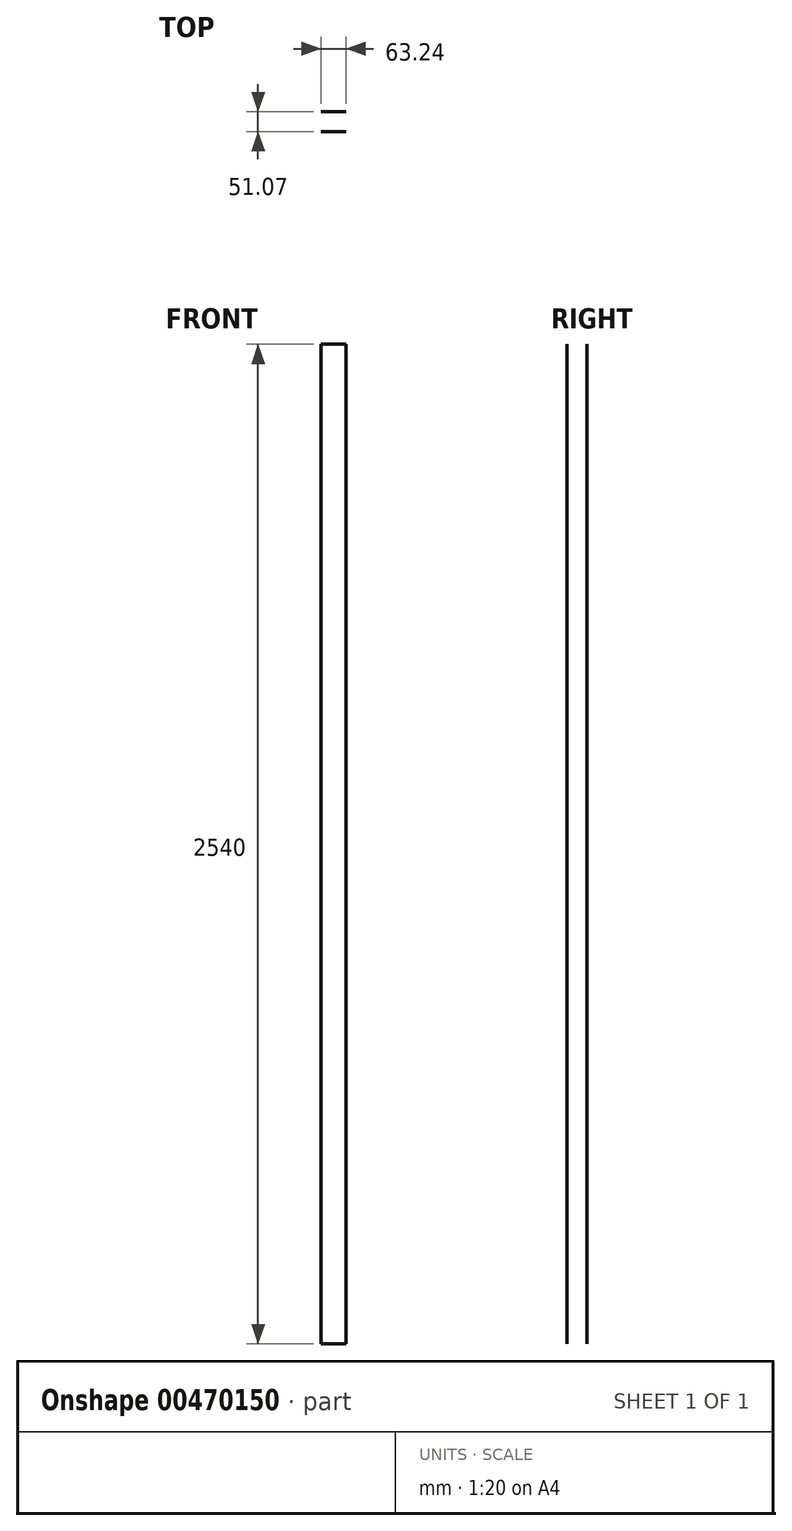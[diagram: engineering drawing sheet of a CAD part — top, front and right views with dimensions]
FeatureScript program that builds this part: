
annotation { "Feature Type Name" : "Feature", "Feature Type Description" : "" }
export const myFeature = defineFeature(function(context is Context, id is Id, definition is map)
    precondition{}
    {
        {
            var Q0;
            Q0=qCreatedBy(makeId("Top.planeOp"),FACE);
            var sketch = newSketch(context, id + "F0", { "sketchPlane" : qUnion([Q0])});
            skLineSegment(sketch, "E0.bottom", {"start": v(-22.73, -27.35) * mm, "end": v(40.5, -27.35) * mm});
            skLineSegment(sketch, "E0.top", {"start": v(-22.73, 23.72) * mm, "end": v(40.5, 23.72) * mm});
            skLineSegment(sketch, "E0.left", {"start": v(-22.73, -27.35) * mm, "end": v(-22.73, 23.72) * mm});
            skLineSegment(sketch, "E0.right", {"start": v(40.5, -27.35) * mm, "end": v(40.5, 23.72) * mm});
            skSolve(sketch);
        }
        {
            var Q0;
            Q0=sQuery(id+"F0.wireOp",EDGE,"E0.bottom");
            var Q1;
            Q1=sQuery(id+"F0.wireOp",EDGE,"E0.top");
            extrude(context, id + "F1", {"bodyType" : ToolBodyType.SURFACE, "surfaceEntities" : qUnion([Q0, Q1]), "oppositeDirection" : true, "depth" : 2540 * mm});
        }
    });
